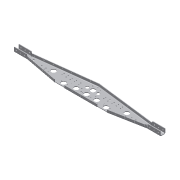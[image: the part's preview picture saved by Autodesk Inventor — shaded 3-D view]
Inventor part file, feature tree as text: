
AUTODESK INVENTOR PART (.ipt)
format: ipt  version: 2013 (Build 170138000, 138)  size: 347,136 bytes
history: native  units: in
note: dims shown in document units (in); Inventor stores cm internally (conversion verified against a paired STEP export)
features: other x2, projected_geometry x2, move_body x1, sketch x1, imported_body x1
ambient origin geometry x8: Origin, YZ Plane, XZ Plane, XY Plane, X Axis, Y Axis, Z Axis, Center Point
feature tree (7):
  other  "Cut-Extrude19"
  other  "446 Drive Plate v41"
  move_body  "Move Body1"
  sketch  "Sketch1"  dims[d0=-17.5in d1=0.0in d2=1.9375in d4=0.4844in d6=8.375in]
  imported_body  "Base1"
  projected_geometry  "Projected Loop1"
  projected_geometry  "Projected Loop2"
